# Revit family: NLRS_57_DUA_UN_rectangular firedamper fd25_sacs
name_source: partatom
category: Duct Accessories
units: mm (PartAtom-declared; Revit-internal decimal feet)

## family parameters
Always vertical = Yes
Cut with Voids When Loaded = No
Part Type = Breaks Into
Round Connector Dimension = Use Diameter
Shared = No
Work Plane-Based = No

## types (28) — shared parameters
Article_Codes = FD25_Article_Codes
Assembly Code = 57.70
Blade material = Promatect, 25 or 40mm
Casing material = Galvanized Steel
Description = Rechthoekige brandklep
Factors = FD25_Factors
FireRating = EN 1366-2 and EN 13501-3, 2h
Fuse temperatuur (default) = 72 degrees Celsius
IfcDescription = Rechthoekige brandklep
IfcExportAs = IfcDamperType
IfcExportType = FIREDAMPER
LoadBearing = No
Manufacturer = Solid Air Climate Solutions
Model = Brandklep - Rechthoekig
NLRS_C_content_datum_uitgifte = 17-01-2022
NLRS_C_content_provider = Solid Air Climate Systems
NLRS_C_content_versie = Versie 3.19.00
NLRS_C_description = Rechthoekige brandklep
NLRS_C_niveau ontwikkeling = LOD400
SACS_Dummy = 1
Show Symbol = Yes
URL = https://solid-air.nl
zero-valued in all types: SACS_Index3

## per-type parameters (varying)
| type | SACS_Index1 | SACS_Index2 | SACS_Length_X | SACS_Option_2_Value | SACS_Show_APP | SACS_Show_MF | SACS_X_Offset |
| FD25 O R O | 0 mm  [stored 0 ft] | 0 mm  [stored 0 ft] | 103.5 mm  [stored 0.339567 ft] | 1 | No | No | 128 mm  [stored 0.419948 ft] |
| FD25 O RS O | 0 mm  [stored 0 ft] | 1 mm  [stored 0.00328084 ft] | 103.5 mm  [stored 0.339567 ft] | 1 | No | No | 128 mm  [stored 0.419948 ft] |
| FD25 O EMS-S O | 0 mm  [stored 0 ft] | 2 mm  [stored 0.00656168 ft] | 103.5 mm  [stored 0.339567 ft] | 2 | No | No | 128 mm  [stored 0.419948 ft] |
| FD25 O M24S O | 0 mm  [stored 0 ft] | 3 mm  [stored 0.00984252 ft] | 103.5 mm  [stored 0.339567 ft] | 3 | No | No | 128 mm  [stored 0.419948 ft] |
| FD25 O M230S O | 0 mm  [stored 0 ft] | 4 mm  [stored 0.0131234 ft] | 103.5 mm  [stored 0.339567 ft] | 3 | No | No | 128 mm  [stored 0.419948 ft] |
| FD25 O M24S-ST O | 0 mm  [stored 0 ft] | 5 mm  [stored 0.0164042 ft] | 103.5 mm  [stored 0.339567 ft] | 3 | No | No | 128 mm  [stored 0.419948 ft] |
| FD25 O EX O | 0 mm  [stored 0 ft] | 6 mm  [stored 0.019685 ft] | 103.5 mm  [stored 0.339567 ft] | 4 | No | No | 128 mm  [stored 0.419948 ft] |
| FD25 APP R O | 1 mm  [stored 0.00328084 ft] | 0 mm  [stored 0 ft] | 103.5 mm  [stored 0.339567 ft] | 1 | Yes | No | 128 mm  [stored 0.419948 ft] |
| FD25 APP RS O | 1 mm  [stored 0.00328084 ft] | 1 mm  [stored 0.00328084 ft] | 103.5 mm  [stored 0.339567 ft] | 1 | Yes | No | 128 mm  [stored 0.419948 ft] |
| FD25 APP EMS-S O | 1 mm  [stored 0.00328084 ft] | 2 mm  [stored 0.00656168 ft] | 103.5 mm  [stored 0.339567 ft] | 2 | Yes | No | 128 mm  [stored 0.419948 ft] |
| FD25 APP M24S O | 1 mm  [stored 0.00328084 ft] | 3 mm  [stored 0.00984252 ft] | 103.5 mm  [stored 0.339567 ft] | 3 | Yes | No | 128 mm  [stored 0.419948 ft] |
| FD25 APP M230S O | 1 mm  [stored 0.00328084 ft] | 4 mm  [stored 0.0131234 ft] | 103.5 mm  [stored 0.339567 ft] | 3 | Yes | No | 128 mm  [stored 0.419948 ft] |
| FD25 APP M24S-ST O | 1 mm  [stored 0.00328084 ft] | 5 mm  [stored 0.0164042 ft] | 103.5 mm  [stored 0.339567 ft] | 3 | Yes | No | 128 mm  [stored 0.419948 ft] |
| FD25 APP EX O | 1 mm  [stored 0.00328084 ft] | 6 mm  [stored 0.019685 ft] | 103.5 mm  [stored 0.339567 ft] | 4 | Yes | No | 128 mm  [stored 0.419948 ft] |
| FD25 MF1 R O | 2 mm  [stored 0.00656168 ft] | 0 mm  [stored 0 ft] | 83.5 mm  [stored 0.27395 ft] | 1 | No | Yes | 134.5 mm  [stored 0.441273 ft] |
| FD25 MF1 RS O | 2 mm  [stored 0.00656168 ft] | 1 mm  [stored 0.00328084 ft] | 83.5 mm  [stored 0.27395 ft] | 1 | No | Yes | 134.5 mm  [stored 0.441273 ft] |
| FD25 MF1 EMS-S O | 2 mm  [stored 0.00656168 ft] | 2 mm  [stored 0.00656168 ft] | 83.5 mm  [stored 0.27395 ft] | 2 | No | Yes | 134.5 mm  [stored 0.441273 ft] |
| FD25 MF1 M24S O | 2 mm  [stored 0.00656168 ft] | 3 mm  [stored 0.00984252 ft] | 83.5 mm  [stored 0.27395 ft] | 3 | No | Yes | 134.5 mm  [stored 0.441273 ft] |
| FD25 MF1 M230S O | 2 mm  [stored 0.00656168 ft] | 4 mm  [stored 0.0131234 ft] | 83.5 mm  [stored 0.27395 ft] | 3 | No | Yes | 134.5 mm  [stored 0.441273 ft] |
| FD25 MF1 M24S-ST O | 2 mm  [stored 0.00656168 ft] | 5 mm  [stored 0.0164042 ft] | 83.5 mm  [stored 0.27395 ft] | 3 | No | Yes | 134.5 mm  [stored 0.441273 ft] |
| FD25 MF1 EX O | 2 mm  [stored 0.00656168 ft] | 6 mm  [stored 0.019685 ft] | 83.5 mm  [stored 0.27395 ft] | 4 | No | Yes | 134.5 mm  [stored 0.441273 ft] |
| FD25 MF2 R O | 3 mm  [stored 0.00984252 ft] | 0 mm  [stored 0 ft] | 103.5 mm  [stored 0.339567 ft] | 1 | No | Yes | 123 mm  [stored 0.403543 ft] |
| FD25 MF2 RS O | 3 mm  [stored 0.00984252 ft] | 1 mm  [stored 0.00328084 ft] | 103.5 mm  [stored 0.339567 ft] | 1 | No | Yes | 123 mm  [stored 0.403543 ft] |
| FD25 MF2 EMS-S O | 3 mm  [stored 0.00984252 ft] | 2 mm  [stored 0.00656168 ft] | 103.5 mm  [stored 0.339567 ft] | 2 | No | Yes | 123 mm  [stored 0.403543 ft] |
| FD25 MF2 M24S O | 3 mm  [stored 0.00984252 ft] | 3 mm  [stored 0.00984252 ft] | 103.5 mm  [stored 0.339567 ft] | 3 | No | Yes | 123 mm  [stored 0.403543 ft] |
| FD25 MF2 M230S O | 3 mm  [stored 0.00984252 ft] | 4 mm  [stored 0.0131234 ft] | 103.5 mm  [stored 0.339567 ft] | 3 | No | Yes | 123 mm  [stored 0.403543 ft] |
| FD25 MF2 M24S-ST O | 3 mm  [stored 0.00984252 ft] | 5 mm  [stored 0.0164042 ft] | 103.5 mm  [stored 0.339567 ft] | 3 | No | Yes | 123 mm  [stored 0.403543 ft] |
| FD25 MF2 EX O | 3 mm  [stored 0.00984252 ft] | 6 mm  [stored 0.019685 ft] | 103.5 mm  [stored 0.339567 ft] | 4 | No | Yes | 123 mm  [stored 0.403543 ft] |

note: [stored X ft] marks values corroborated as IEEE doubles in the binary element streams (Revit-internal decimal feet)

## geometry (parser evidence)
native form markers: Sweep x12
no freeform markers — native parametric forms only
